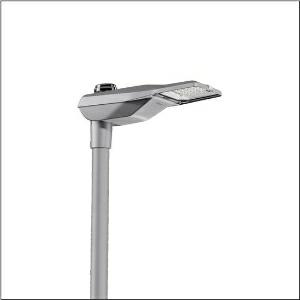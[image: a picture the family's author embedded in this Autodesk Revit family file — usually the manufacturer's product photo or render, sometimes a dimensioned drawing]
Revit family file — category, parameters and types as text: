
# Revit family: streetlight_sl_21_micro___p0_8a_5xe5u67n08cb_86d2
name_source: partatom
category: Lighting Fixtures
units: mm (PartAtom-declared; Revit-internal decimal feet)

## family parameters
Cut with Voids When Loaded = No
Host = Face
Light Source = No
Part Type = Normal
Room Calculation Point = No
Round Connector Dimension = Use Diameter
Shared = No

## types (1)
- --- (1 x LED, 2020 lm, 15.8 W, 2700K)
    Apparent Load = 16 VA
    CIE Flux Codes = 33 69 96 100 100
    Color Rendering = 70
    Color Temperature = 2700K
    Default Elevation = 1800 mm
    Description = Streetlight SL 21 micro, mast luminaire, primary light control with lens, of PMMA, primary optical cover: cover, of toughened safety glass, transparent, light distribution: P0.8a, light emission: direct distribution, primary light characteristic: asymmetric, installation type: post-top, LED, 3G 1.5mm², High Power LED, rated luminous flux: 2.020lm, luminous efficacy: 128lm/W, light colour: 727, colour temperature: 2700K, control gear: NEMA (7pin), control: flexible luminous flux parameterisation, time-dependent luminous flux control, constant luminous flux control, pre-setting: linear dimming characteristic, overheat protection, mains connection: 230..240V, AC, 50/60Hz, connection cable pre-assembled, cable length: 6,5m, wiring characteristics: H07RN-F, start of lifetime: 16W, end of service life: 16W, reduction: 8W, luminaire housing, of diecast aluminium (EN AC-44300), powder-coated, SITECO metallic grey (DB 702S), corrosivity category C5 high according to DIN EN ISO 12944, multi-level sealing system, sealing non-destructively replaceable, inclination adjustable: 0°, 5°, 10°, 15°, length: 528mm, width: 235mm, height: 110mm, spigot size: 76/60mm (post-top), mounting height: 4..8m, protection rating (complete): IP66, insulation class (complete): insulation class I (protective earthing), certification: CE, ENEC, ENEC+, VDE, impact resistance: IK10, permissible operating ambient temperature for outdoor applications: -40..+50°C, standard-compliant lighting for roads and squares, packaging unit: 1 piece

Light Distribution: P0.8a
    Height = 110 mm
    Lamp = 1 x LED
    Lamp Light Flux = 2020 lm
    Lamp Power = 15.8 W
    Lamp count = 1
    Length = 528 mm
    Luminous efficacy = 128 lm/W
    Manufacturer = Siteco
    ModVariant = No
    Model = 5XE5U67N08CB
    Number of Poles = 1
    OnlyDefault = Yes
    Power Factor = 1
    Product Name = Streetlight SL 21 micro | P0.8a
    Product group = mast luminaire | pylon top
    ProductGroupID = 6100
    Protection Class = Protection class I
    Protection Degree = IP 66
    RLX_Detail_Level = 1
    RLX_Emergency_Light_Flux = 0 lm
    RLX_Emergency_Type = 0
    RLX_Emergency_Type_DB = No
    RlxData = <blob elided: 98585 chars, md5=eb37c469>
    Socket = socket
    Standby Power = 0 W
    System Light Flux = 2020 lm
    System Power = 16 W
    Type Comments = factory setting: luminous flux: 100 % | dim-lin: 254 | 300 mA
    Type Image = l_1294375.jpg
    URL = http://relux.com
    VarID = @adj_081439
    Voltage = 0 V
    Weight = 0.00 kg
    Width = 235 mm

## geometry (parser evidence)
native form markers: Blend x4, Sweep x10
no freeform markers — native parametric forms only
